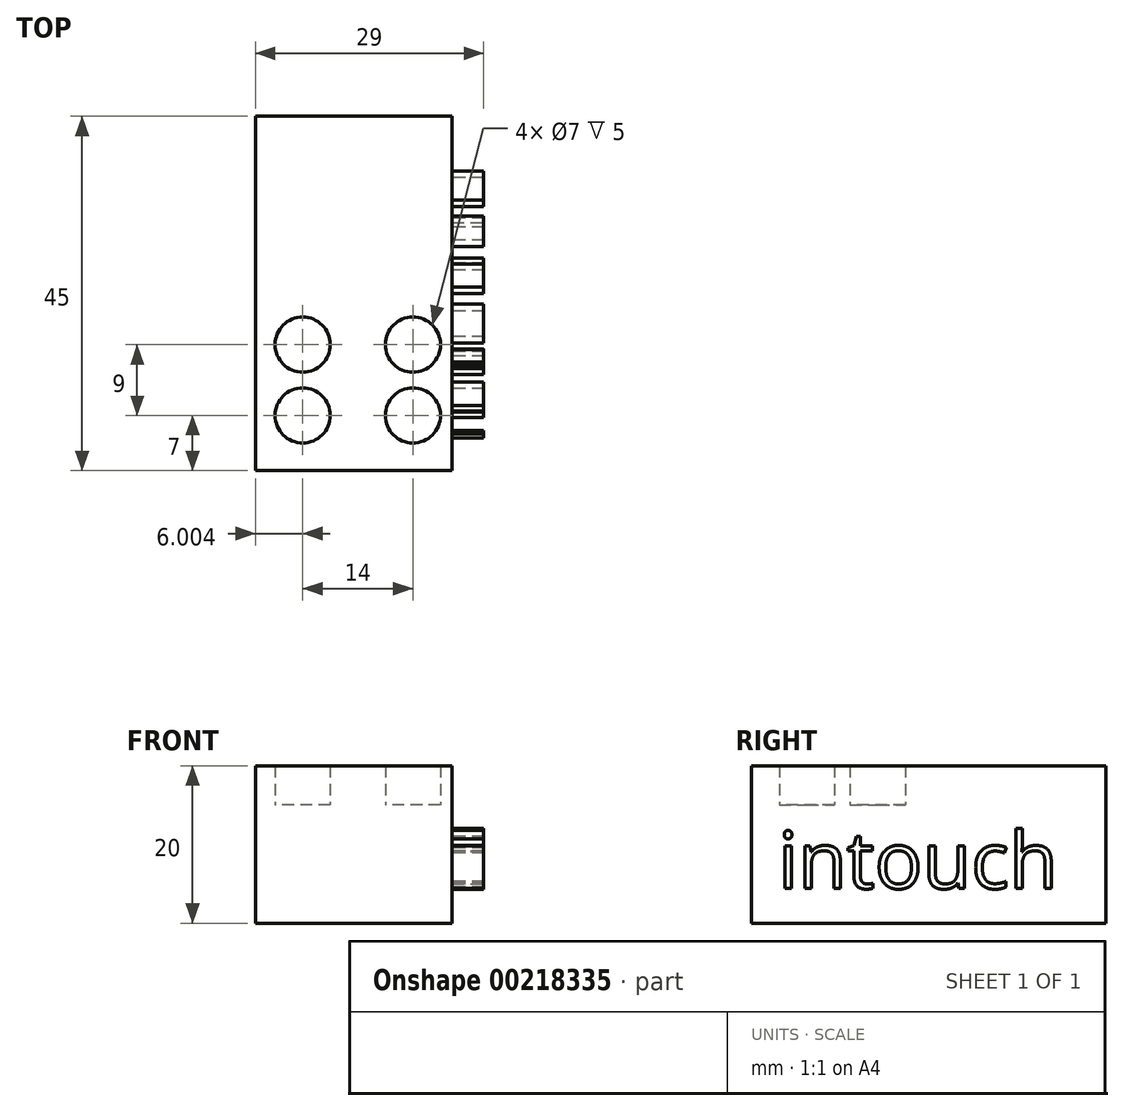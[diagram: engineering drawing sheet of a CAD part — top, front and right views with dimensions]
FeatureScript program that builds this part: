
annotation { "Feature Type Name" : "Feature", "Feature Type Description" : "" }
export const myFeature = defineFeature(function(context is Context, id is Id, definition is map)
    precondition{}
    {
        {
            var Q0;
            Q0=qCreatedBy(makeId("Top.planeOp"),FACE);
            var sketch = newSketch(context, id + "F0", { "sketchPlane" : qUnion([Q0])});
            skLineSegment(sketch, "E0", {"start": v(-13.18, 26.43) * mm, "end": v(11.82, 26.43) * mm});
            skLineSegment(sketch, "E1", {"start": v(11.82, 26.43) * mm, "end": v(11.82, -18.57) * mm});
            skLineSegment(sketch, "E2", {"start": v(-13.18, -18.57) * mm, "end": v(-13.18, 26.43) * mm});
            skLineSegment(sketch, "E3", {"start": v(-13.18, -18.57) * mm, "end": v(11.82, -18.57) * mm});
            skSolve(sketch);
        }
        {
            var Q0;
            Q0=makeQuery(id+"F0.imprint","IMPRINT",FACE,{"disambiguationData":[TD([[makeQuery(id+"F0.imprint","IMPRINT",EDGE,{"derivedFrom":sQuery(id+"F0.wireOp",EDGE,"E0")}),-1.0]])]});
            extrude(context, id + "F1", {"entities" : qUnion([Q0]), "depth" : 15 * mm});
        }
        {
            var Q0;
            Q0=makeQuery(id+"F1.opExtrude","CAP_FACE",FACE,{"disambiguationData":[OSD([sQuery(id+"F0.wireOp",EDGE,"E0"),sQuery(id+"F0.wireOp",EDGE,"E1"),sQuery(id+"F0.wireOp",EDGE,"E2"),sQuery(id+"F0.wireOp",EDGE,"E3")])],"isStart":false});
            var sketch = newSketch(context, id + "F2", { "sketchPlane" : qUnion([Q0])});
            skCircle(sketch, "E4", {"center": v(-7.18, 19.43) * mm, "radius": 3.5 * mm});
            skCircle(sketch, "E5", {"center": v(6.82, 19.43) * mm, "radius": 3.5 * mm});
            skCircle(sketch, "E6", {"center": v(-7.18, 10.43) * mm, "radius": 3.5 * mm});
            skCircle(sketch, "E7", {"center": v(6.82, 10.43) * mm, "radius": 3.5 * mm});
            skLineSegment(sketch, "E8.0", {"start": v(-13.18, -18.57) * mm, "end": v(-13.18, 26.43) * mm});
            skLineSegment(sketch, "E9", {"start": v(-13.18, 3.93) * mm, "end": v(53.09, 3.93) * mm, "construction": true});
            skCircle(sketch, "E10.MirrorC", {"center": v(6.82, -2.57) * mm, "radius": 3.5 * mm});
            skCircle(sketch, "E11.MirrorC", {"center": v(6.82, -11.57) * mm, "radius": 3.5 * mm});
            skCircle(sketch, "E12.MirrorC", {"center": v(-7.18, -11.57) * mm, "radius": 3.5 * mm});
            skCircle(sketch, "E13.MirrorC", {"center": v(-7.18, -2.57) * mm, "radius": 3.5 * mm});
            skSolve(sketch);
        }
        {
            var Q0;
            Q0=makeQuery(id+"F2.imprint","IMPRINT",FACE,{"disambiguationData":[TD([[makeQuery(id+"F2.imprint","IMPRINT",EDGE,{"derivedFrom":sQuery(id+"F2.wireOp",EDGE,"E4")}),1.0]])]});
            var Q1;
            Q1=makeQuery(id+"F2.imprint","IMPRINT",FACE,{"disambiguationData":[TD([[makeQuery(id+"F2.imprint","IMPRINT",EDGE,{"derivedFrom":sQuery(id+"F2.wireOp",EDGE,"E6")}),1.0]])]});
            var Q2;
            Q2=makeQuery(id+"F2.imprint","IMPRINT",FACE,{"disambiguationData":[TD([[makeQuery(id+"F2.imprint","IMPRINT",EDGE,{"derivedFrom":sQuery(id+"F2.wireOp",EDGE,"E7")}),1.0]])]});
            var Q3;
            Q3=makeQuery(id+"F2.imprint","IMPRINT",FACE,{"disambiguationData":[TD([[makeQuery(id+"F2.imprint","IMPRINT",EDGE,{"derivedFrom":sQuery(id+"F2.wireOp",EDGE,"E5")}),1.0]])]});
            var Q4;
            Q4=makeQuery(id+"F2.imprint","IMPRINT",FACE,{"disambiguationData":[TD([[makeQuery(id+"F2.imprint","IMPRINT",EDGE,{"derivedFrom":sQuery(id+"F2.wireOp",EDGE,"E10.MirrorC")}),-1.0]])]});
            var Q5;
            Q5=makeQuery(id+"F2.imprint","IMPRINT",FACE,{"disambiguationData":[TD([[makeQuery(id+"F2.imprint","IMPRINT",EDGE,{"derivedFrom":sQuery(id+"F2.wireOp",EDGE,"E11.MirrorC")}),-1.0]])]});
            var Q6;
            Q6=makeQuery(id+"F2.imprint","IMPRINT",FACE,{"disambiguationData":[TD([[makeQuery(id+"F2.imprint","IMPRINT",EDGE,{"derivedFrom":sQuery(id+"F2.wireOp",EDGE,"E12.MirrorC")}),-1.0]])]});
            var Q7;
            Q7=makeQuery(id+"F2.imprint","IMPRINT",FACE,{"disambiguationData":[TD([[makeQuery(id+"F2.imprint","IMPRINT",EDGE,{"derivedFrom":sQuery(id+"F2.wireOp",EDGE,"E13.MirrorC")}),-1.0]])]});
            extrude(context, id + "F3", {"entities" : qUnion([Q0, Q1, Q2, Q3, Q4, Q5, Q6, Q7]), "operationType" : NewBodyOperationType.ADD, "depth" : 5 * mm});
        }
        {
            var Q0;
            Q0=makeQuery(id+"F1.opExtrude","SWEPT_FACE",FACE,{"disambiguationData":[OSD([sQuery(id+"F0.wireOp",EDGE,"E1")])]});
            var sketch = newSketch(context, id + "F4", { "sketchPlane" : qUnion([Q0])});
            skSolve(sketch);
        }
        {
            var Q0;
            {var subQ0=sQuery(id+"F0.wireOp",EDGE,"E1");Q0=makeQuery(id+"F4.imprint","IMPRINT",FACE,{"disambiguationData":[TD([[makeQuery(id+"F4.imprint","IMPRINT",EDGE,{"derivedFrom":makeQuery(id+"F1.opExtrude","CAP_EDGE",EDGE,{"disambiguationData":[OSD([subQ0])],"isStart":true})}),-1.0]])]});}
            var sketch = newSketch(context, id + "F5", { "sketchPlane" : qUnion([Q0])});
            skText(sketch, "E14", { "text": "intouch", "fontName": "OpenSans-Regular.ttf"});
            const initialGuessF5  = {"E14": [-0.01523, 0.0044, 1, 0, 0.00725]};
            skSetInitialGuess(sketch, initialGuessF5);
            skSolve(sketch);
        }
        {
            var Q0;
            Q0 = qSketchRegion(id + "F5", true);
            extrude(context, id + "F6", {"entities" : qUnion([Q0]), "operationType" : NewBodyOperationType.ADD, "depth" : 4 * mm});
        }
    });
